# Revit family: Furniture_Office-Chairs_Flokk_HAG_Capisco-Puls_8010
name_source: partatom
category: Furniture
units: mm (PartAtom-declared; Revit-internal decimal feet)

## family parameters
Always vertical = Yes
Cut with Voids When Loaded = No
OmniClass Number = 23.40.20.14.14.11
OmniClass Title = Chairs
Room Calculation Point = No
Shared = No
Work Plane-Based = No

## types (1)
- HAG Capisco Puls 8010
    AssetType = Movable
    BIMObjectName = Furniture_Office-Chairs_Flokk_HAG_Capisco-Puls_8010
    Brand = HAG
    Category = Task Chairs
    Collection = Capisco
    Color = Available in all the HÅG Total Colour Standard and Extended textiles (except in leather and Steelcut Trio)
    Cost = 0 $
    Default Elevation = 0 mm  [stored 0 ft]
    Description = The HÅG Capisco Puls provides you with all the benefits of the HÅG Capisco, except that it’s lighter. For lively environments such as creative workplaces, it’s a versatile choice. It’s easy to wipe down, and like the HÅG Capisco, perfectly suits height adjustable desks.
    Designer = Peter Opsvik
    DurationUnit = Year
    EnergyConsumption = 607 MJ
    Features = HÅG inBalance® (balanced, flowing tilt function)

Adjustable tilt tension backwards

Seat height adjustment

Seat depth adjustment

Back height adjustment

Lockable seat

Five star base (Ø730 mm) in aluminium with curved/arched footplates.
    Finish = The HÅG Capisco Puls 8010 is a plastic chair with an integrated seat cushion for improved comfort. The saddle seat can be adjusted between low and high working positions, all the way up to a standing position, enabling you to be more dynamic in your movements while still sitting in a balanced position.
    GlobalWarming = 31 kg CO2-equ.
    HighestSeatingHeight = 795 mm  [stored 2.60827 ft]
    IfcExportAs = IfcFurnishingElementType
    IfcExportType = CHAIR
    LowestSeatingHeight = 389 mm  [stored 1.27625 ft]
    MainColor = Various
    Manufacturer = Flokk
    ManufacturerName = Flokk
    ManufacturerURL = https://www.flokk.com
    Material = Textile, metal, plastic
    Model = HAG Capisco Puls 8010
    ModelNumber = 8010
    NBSDescription = Office chairs
    NBSReference = 45-35-20/330
    Name = HAG_Capisco-Puls_8010
    NominalDepth = 667 mm  [stored 2.18832 ft]
    NominalHeight = 1005 mm  [stored 3.29724 ft]
    NominalLength = 730 mm  [stored 2.39501 ft]
    OfficeChairTertiaryMaterial = Plastic Black
    ProductInformation = The HÅG Capisco Puls provides you with all the benefits of the HÅG Capisco, except that it’s lighter. For lively environments such as creative workplaces, it’s a versatile choice. It’s easy to wipe down, and like the HÅG Capisco, perfectly suits height adjustable desks.
    Revision = 4
    SeatingHeight = 560 mm  [stored 1.83727 ft]
    ShareRecyclableMaterials = 95%
    ShareRecycledMaterials = 48%
    Size = 730x730x830/1250mm
    URL = https://store.flokk.com
    Uniclass2 = Pr_40_50_12_57
    Uniclass2015Description = Office chairs
    Uniclass2015Reference = Pr_40_50_12_57
    Version = 2
    VersionDate = 07/11/2022
    WarrantyDurationUnit = Year

note: [stored X ft] marks values corroborated as IEEE doubles in the binary element streams (Revit-internal decimal feet)

## geometry (parser evidence)
native form markers: Sweep x11
no freeform markers — native parametric forms only
